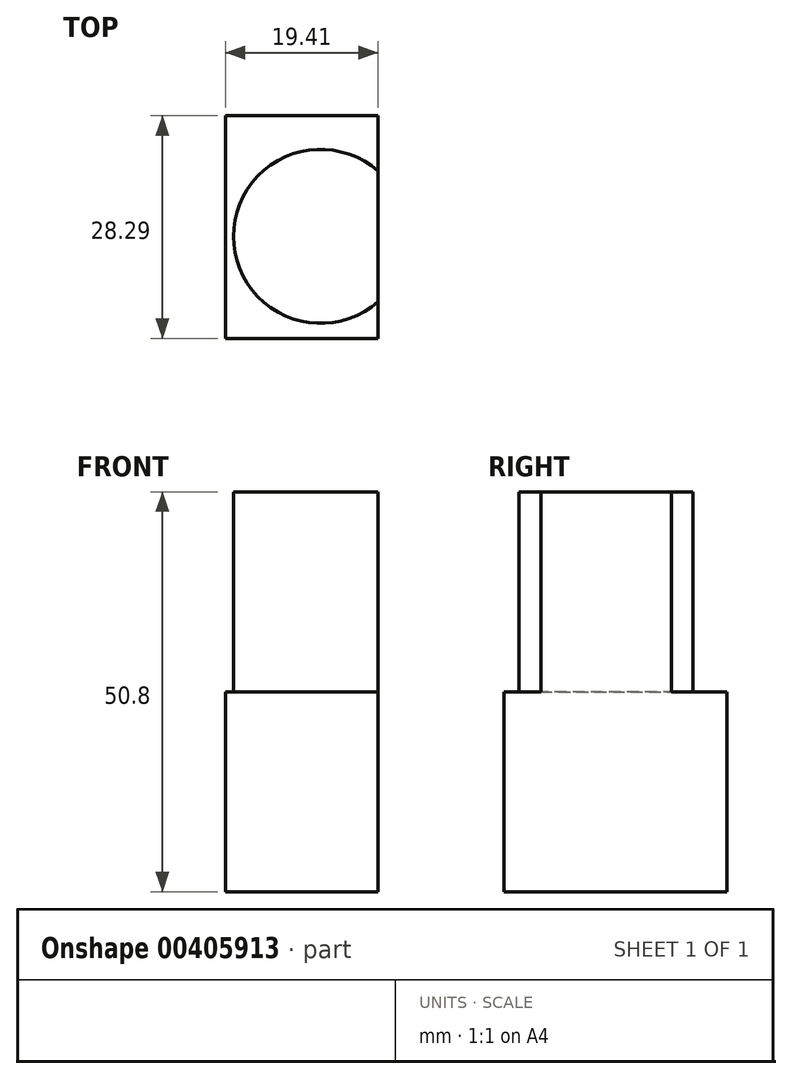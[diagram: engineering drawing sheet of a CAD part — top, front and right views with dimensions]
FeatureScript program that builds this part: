
annotation { "Feature Type Name" : "Feature", "Feature Type Description" : "" }
export const myFeature = defineFeature(function(context is Context, id is Id, definition is map)
    precondition{}
    {
        {
            var Q0;
            Q0=qCreatedBy(makeId("Top.planeOp"),FACE);
            var sketch = newSketch(context, id + "F0", { "sketchPlane" : qUnion([Q0])});
            skLineSegment(sketch, "E0.bottom", {"start": v(0, 0) * mm, "end": v(-19.41, 0) * mm});
            skLineSegment(sketch, "E0.top", {"start": v(0, 28.3) * mm, "end": v(-19.41, 28.3) * mm});
            skLineSegment(sketch, "E0.left", {"start": v(0, 0) * mm, "end": v(0, 28.3) * mm});
            skLineSegment(sketch, "E0.right", {"start": v(-19.41, 0) * mm, "end": v(-19.41, 28.3) * mm});
            skSolve(sketch);
        }
        {
            var Q0;
            Q0=makeQuery(id+"F0.imprint","IMPRINT",FACE,{"disambiguationData":[TD([[makeQuery(id+"F0.imprint","IMPRINT",EDGE,{"derivedFrom":sQuery(id+"F0.wireOp",EDGE,"E0.bottom")}),-1.0]])]});
            extrude(context, id + "F1", {"entities" : qUnion([Q0]), "depth" : 25.4 * mm});
        }
        {
            var Q0;
            Q0=makeQuery(id+"F1.opExtrude","CAP_FACE",FACE,{"disambiguationData":[OSD([sQuery(id+"F0.wireOp",EDGE,"E0.bottom"),sQuery(id+"F0.wireOp",EDGE,"E0.top"),sQuery(id+"F0.wireOp",EDGE,"E0.left"),sQuery(id+"F0.wireOp",EDGE,"E0.right")])],"isStart":false});
            var sketch = newSketch(context, id + "F2", { "sketchPlane" : qUnion([Q0])});
            skCircle(sketch, "E1", {"center": v(-7.32, 12.97) * mm, "radius": 11.05 * mm});
            skSolve(sketch);
        }
        {
            var Q0;
            {var subQ0=sQuery(id+"F2.wireOp",EDGE,"E1");var subQ1=makeQuery(id+"F1.opExtrude","CAP_EDGE",EDGE,{"disambiguationData":[OSD([sQuery(id+"F0.wireOp",EDGE,"E0.left")])],"isStart":false});var subQ2=makeQuery(id+"F2.imprint","INTERSECT",VERTEX,{"disambiguationData":[OD(0.0)],"derivedFrom":[subQ1,subQ0]});Q0=makeQuery(id+"F2.imprint","IMPRINT",FACE,{"disambiguationData":[TD([[makeQuery(id+"F2.imprint","IMPRINT",EDGE,{"disambiguationData":[TD([[subQ2,1.0]])],"derivedFrom":subQ0}),1.0]])]});}
            extrude(context, id + "F3", {"entities" : qUnion([Q0]), "operationType" : NewBodyOperationType.ADD, "depth" : 25.4 * mm});
        }
    });
